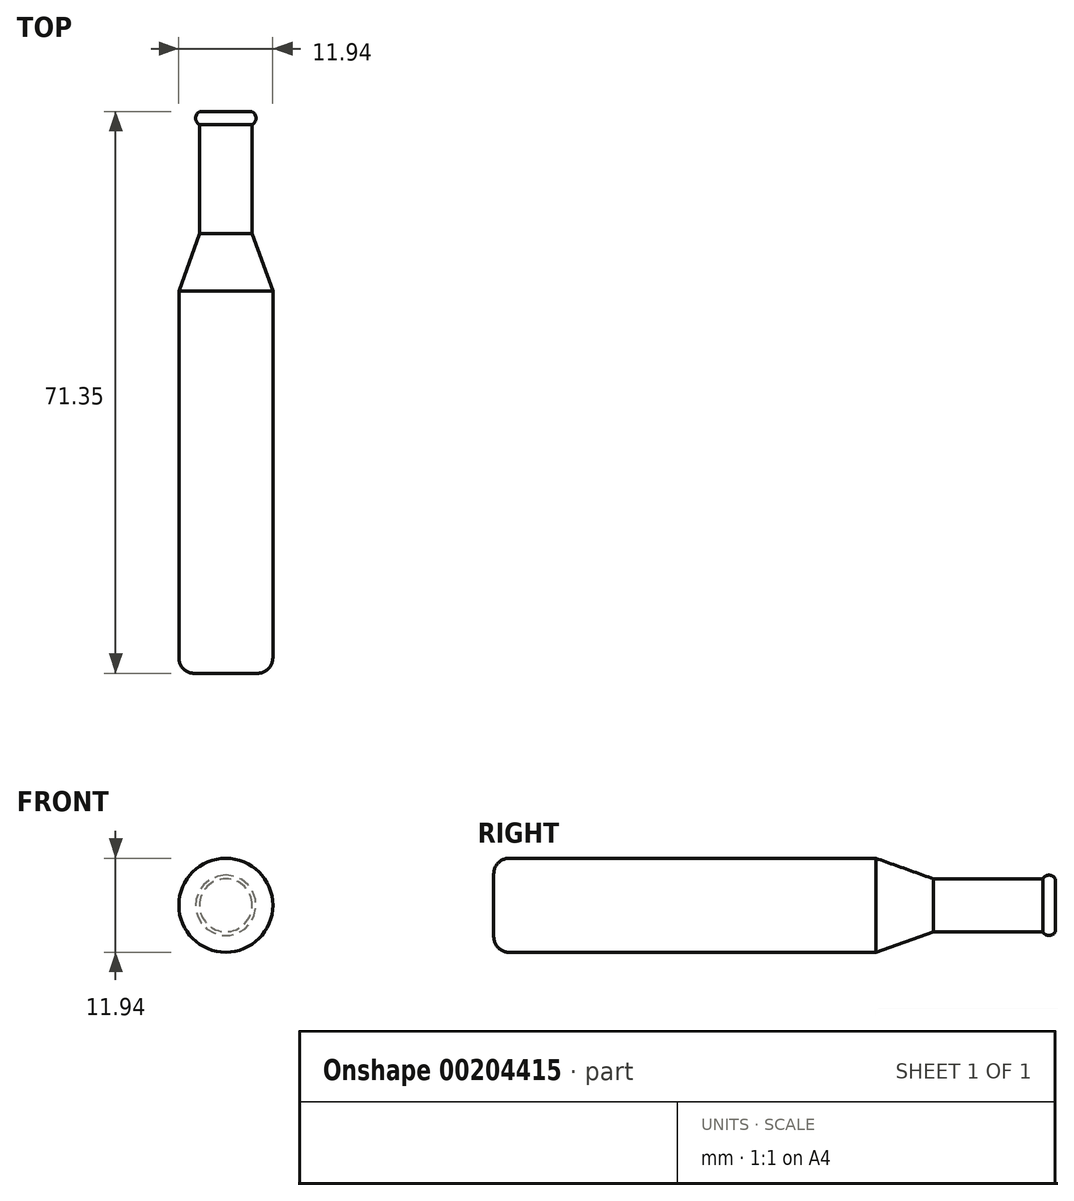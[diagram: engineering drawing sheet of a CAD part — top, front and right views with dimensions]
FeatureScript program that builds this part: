
annotation { "Feature Type Name" : "Feature", "Feature Type Description" : "" }
export const myFeature = defineFeature(function(context is Context, id is Id, definition is map)
    precondition{}
    {
        {
            var Q0;
            Q0=qCreatedBy(makeId("Top.planeOp"),FACE);
            var sketch = newSketch(context, id + "F0", { "sketchPlane" : qUnion([Q0])});
            skLineSegment(sketch, "E0.right", {"start": v(-21.07, 15.4) * mm, "end": v(-21.07, -27.78) * mm});
            skLineSegment(sketch, "E1", {"start": v(-21.07, 15.4) * mm, "end": v(-21.07, 28.1) * mm});
            skLineSegment(sketch, "E2", {"start": v(-21.07, 28.1) * mm, "end": v(-24.42, 28.1) * mm});
            skLineSegment(sketch, "E3", {"start": v(-27.04, -27.78) * mm, "end": v(-21.07, -27.78) * mm});
            skLineSegment(sketch, "E4", {"start": v(-27.04, -27.78) * mm, "end": v(-27.04, 20.75) * mm});
            skLineSegment(sketch, "E5", {"start": v(-27.04, 20.75) * mm, "end": v(-24.42, 28.1) * mm});
            skLineSegment(sketch, "E6", {"start": v(-21.07, 43.57) * mm, "end": v(-24.42, 43.57) * mm});
            skLineSegment(sketch, "E7", {"start": v(-24.42, 28.1) * mm, "end": v(-24.42, 43.57) * mm});
            skLineSegment(sketch, "E8", {"start": v(-21.07, 43.57) * mm, "end": v(-21.07, 28.1) * mm});
            skArc(sketch, "E9", {"start": v(-24.42, 43.57) * mm, "mid": v(-24.9, 42.76) * mm, "end": v(-24.42, 41.95) * mm});
            skSolve(sketch);
        }
        {
            var Q0;
            Q0 = qSketchRegion(id + "F0", true);
            var Q1;
            Q1=sQuery(id+"F0.wireOp",EDGE,"E0.right");
            revolve(context, id + "F1", {"entities" : qUnion([Q0]), "axis" : qUnion([Q1]), "revolveType" : RevolveType.FULL});
        }
        {
            var Q0;
            Q0=makeQuery(id+"F1.opRevolve","SWEPT_EDGE",EDGE,{"disambiguationData":[OSD([sQuery(id+"F0.wireOp",EDGE,"E3"),sQuery(id+"F0.wireOp",EDGE,"E4")])]});
            fillet(context, id + "F2", {"entities" : qUnion([Q0]), "radius" : 1.96 * mm, "allowEdgeOverflow" : false});
        }
    });
